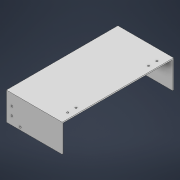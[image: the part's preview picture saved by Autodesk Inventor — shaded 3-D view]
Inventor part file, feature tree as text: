
AUTODESK INVENTOR PART (.ipt)
format: ipt  version: 2021 (Build 250183000, 183)  size: 160,256 bytes
history: native  units: mm
features: extrude x7, sketch x7
ambient origin geometry x8: Origin, YZ Plane, XZ Plane, XY Plane, X Axis, Y Axis, Z Axis, Center Point
bodies: Volumenkörper1 (feature_tree)
feature tree (14):
  extrude  "Extrusion1"  Depth=200.0mm
  extrude  "Extrusion3"  Depth=2.0mm
  extrude  "Extrusion4"  Depth=48.0mm TaperAngle=0.0deg
  extrude  "Extrusion5"  Depth=3.2mm
  extrude  "Extrusion6"  Depth=15.0mm
  extrude  "Extrusion7"  Depth=10.0mm
  extrude  "Extrusion8"  Depth=50.0mm
  sketch  "Skizze1"  dims[d0=100.0mm d1=200.0mm]
  sketch  "Skizze3"  dims[d2=2.0mm d3=0.0mm d8=2.0mm]
  sketch  "Skizze4"  dims[d9=2.0mm d10=48.0mm d11=0.0mm]
  sketch  "Skizze5"  dims[d12=3.2mm d13=3.2mm]
  sketch  "Skizze6"  dims[d14=15.0mm d15=15.0mm]
  sketch  "Skizze7"  dims[d16=10.0mm d17=10.0mm]
  sketch  "Skizze8"  dims[d18=50.0mm d19=0.0mm d20=3.2mm d21=3.2mm d22=10.0mm d23=10.0mm d24=15.0mm d25=15.0mm d26=50.0mm d27=0.0mm d31=3.2mm d32=3.2mm d33=3.2mm d34=3.2mm d35=10.0mm d36=10.0mm d37=15.0mm d38=10.0mm d39=10.0mm d40=15.0mm d41=20.0mm d42=20.0mm d43=2.0mm d44=0.0mm d45=3.2mm d46=25.0mm d47=5.0mm d48=2.0mm d49=0.0mm d50=3.2mm d51=25.0mm d52=5.0mm d53=50.0mm d54=0.0mm]
